# Revit family: Toilet-Round_Front-Dual_Flush-Right_Height-American_Standard-Edgemere-204BA200
name_source: partatom
category: Plumbing Fixtures
revit_build: Autodesk Revit 2014 (Build: 20130308_1515(x64)
units: mm (PartAtom-declared; Revit-internal decimal feet)

## types (1)
- 204BA200
    ADA Compliant = Yes
    Assembly Code = D2010110
    Bowl Shape = Round Front
    CW Connection = Yes
    CWFU = 3
    Cold Water Connection Diameter = 1/2"
    Cold Water Connection Height = 8"
    Cold Water Connection Radius = 1/4"
    Cold Water Connection Width = 6"
    Default Elevation = 0"
    Description = 204BA200 Edgemere Right Height Round Front Dual Flush  12" Rough Toilet
    EPA WaterSense = Yes
    EverClean Surface = Yes
    Finish = Vitreous China-American Standard-020-White
    Flush Rate = 1.28Gpf (4.8Lpf)
    HW Connection = No
    HWFU = 0
    Height = 31 1/8"
    Installation Type = Floor Mounted
    Length = 28 3/16"
    Manufacturer = American Standard
    Material = Vitreous China-American Standard-020-White
    Model = 204BA200
    Price = Prices may vary. Please consult Manufacturer Representative for most up-to-date price list.
    Product Documentation Link = https://www.americanstandard-us.com
    Product URL = https://www.americanstandard-us.com
    URL = http://www.americanstandard-us.com
    Vent Connection = No
    WFU = 3
    Warranty Information = 5 Year Limited
    Waste Connection = Yes
    Waste Connection Diameter = 2"
    Waste Connection Radius = 1"
    Width = 17"

## geometry (parser evidence)
native form markers: Sweep x2
no freeform markers — native parametric forms only
